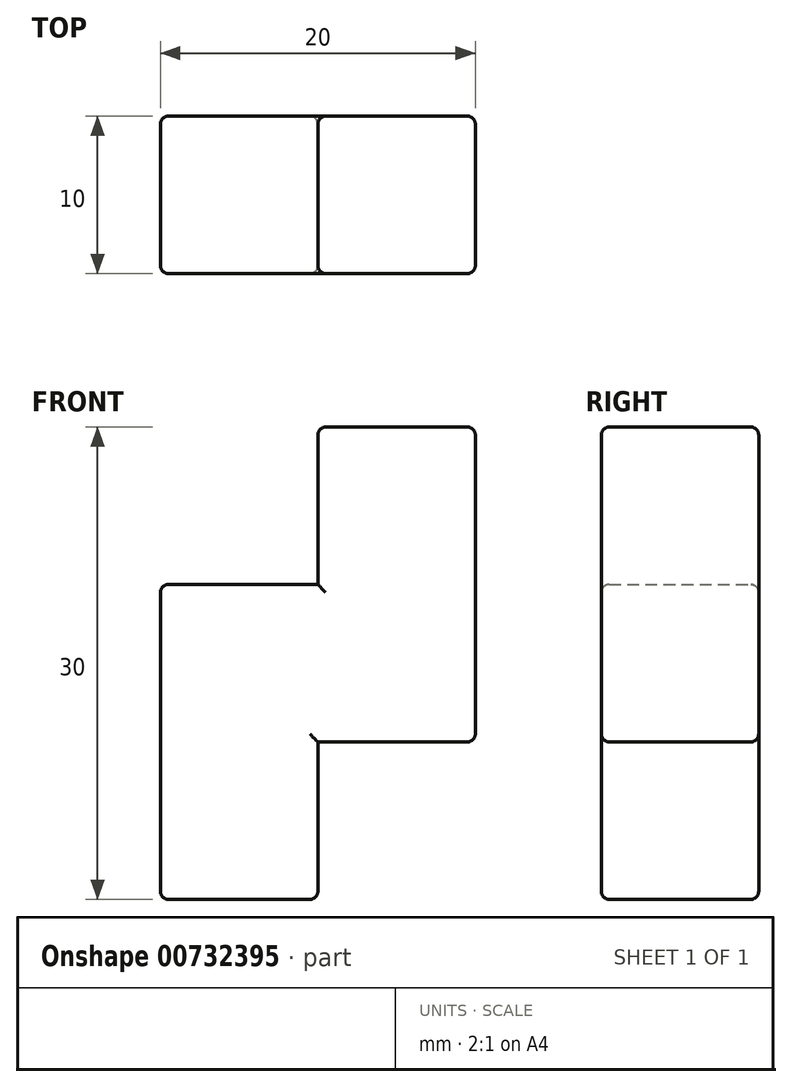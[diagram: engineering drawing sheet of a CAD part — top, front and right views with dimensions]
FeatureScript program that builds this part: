
annotation { "Feature Type Name" : "Feature", "Feature Type Description" : "" }
export const myFeature = defineFeature(function(context is Context, id is Id, definition is map)
    precondition{}
    {
        {
            var Q0;
            Q0=qCreatedBy(makeId("Front.planeOp"),FACE);
            var sketch = newSketch(context, id + "F0", { "sketchPlane" : qUnion([Q0])});
            skLineSegment(sketch, "E0.bottom", {"start": v(-10, -5) * mm, "end": v(10, -5) * mm});
            skLineSegment(sketch, "E0.top", {"start": v(-10, 5) * mm, "end": v(10, 5) * mm});
            skLineSegment(sketch, "E0.left", {"start": v(-10, -5) * mm, "end": v(-10, 5) * mm});
            skLineSegment(sketch, "E0.right", {"start": v(10, -5) * mm, "end": v(10, 5) * mm});
            skPoint(sketch, "E0.middle", {"position": v(0, 0) * mm});
            skLineSegment(sketch, "E1", {"start": v(10, 5) * mm, "end": v(10, 15) * mm});
            skLineSegment(sketch, "E2", {"start": v(10, 15) * mm, "end": v(0, 15) * mm});
            skLineSegment(sketch, "E3", {"start": v(0, 15) * mm, "end": v(0, 5) * mm});
            skLineSegment(sketch, "E4", {"start": v(-10, -5) * mm, "end": v(-10, -15) * mm});
            skLineSegment(sketch, "E5", {"start": v(-10, -15) * mm, "end": v(0, -15) * mm});
            skLineSegment(sketch, "E6", {"start": v(0, -15) * mm, "end": v(0, -5) * mm});
            skSolve(sketch);
        }
        {
            var Q0;
            Q0 = qSketchRegion(id + "F0", true);
            extrude(context, id + "F1", {"entities" : qUnion([Q0]), "depth" : 10 * mm, "offsetDistance" : 25 * mm});
        }
        {
            var Q0;
            Q0=makeQuery(id+"F1.opExtrude","CAP_FACE",FACE,{"disambiguationData":[OSD([sQuery(id+"F0.wireOp",EDGE,"E0.bottom"),sQuery(id+"F0.wireOp",EDGE,"E0.top"),sQuery(id+"F0.wireOp",EDGE,"E0.left"),sQuery(id+"F0.wireOp",EDGE,"E0.right"),sQuery(id+"F0.wireOp",EDGE,"E1"),sQuery(id+"F0.wireOp",EDGE,"E2"),sQuery(id+"F0.wireOp",EDGE,"E3"),sQuery(id+"F0.wireOp",EDGE,"E4"),sQuery(id+"F0.wireOp",EDGE,"E5"),sQuery(id+"F0.wireOp",EDGE,"E6")])],"isStart":true});
            var Q1;
            Q1=makeQuery(id+"F1.opExtrude","CAP_FACE",FACE,{"disambiguationData":[OSD([sQuery(id+"F0.wireOp",EDGE,"E0.bottom"),sQuery(id+"F0.wireOp",EDGE,"E0.top"),sQuery(id+"F0.wireOp",EDGE,"E0.left"),sQuery(id+"F0.wireOp",EDGE,"E0.right"),sQuery(id+"F0.wireOp",EDGE,"E1"),sQuery(id+"F0.wireOp",EDGE,"E2"),sQuery(id+"F0.wireOp",EDGE,"E3"),sQuery(id+"F0.wireOp",EDGE,"E4"),sQuery(id+"F0.wireOp",EDGE,"E5"),sQuery(id+"F0.wireOp",EDGE,"E6")])],"isStart":false});
            var Q2;
            Q2=makeQuery(id+"F1.opExtrude","SWEPT_FACE",FACE,{"disambiguationData":[OSD([sQuery(id+"F0.wireOp",EDGE,"E5")])]});
            var Q3;
            Q3=makeQuery(id+"F1.opExtrude","SWEPT_FACE",FACE,{"disambiguationData":[OSD([sQuery(id+"F0.wireOp",EDGE,"E0.right"),sQuery(id+"F0.wireOp",EDGE,"E1")])]});
            var Q4;
            Q4=makeQuery(id+"F1.opExtrude","SWEPT_FACE",FACE,{"disambiguationData":[OSD([sQuery(id+"F0.wireOp",EDGE,"E2")])]});
            var Q5;
            Q5=makeQuery(id+"F1.opExtrude","SWEPT_FACE",FACE,{"disambiguationData":[OSD([sQuery(id+"F0.wireOp",EDGE,"E0.left"),sQuery(id+"F0.wireOp",EDGE,"E4")])]});
            fillet(context, id + "F2", {"entities" : qUnion([Q0, Q1, Q2, Q3, Q4, Q5]), "radius" : 0.5 * mm, "tangentPropagation" : true, "allowEdgeOverflow" : false});
        }
    });
